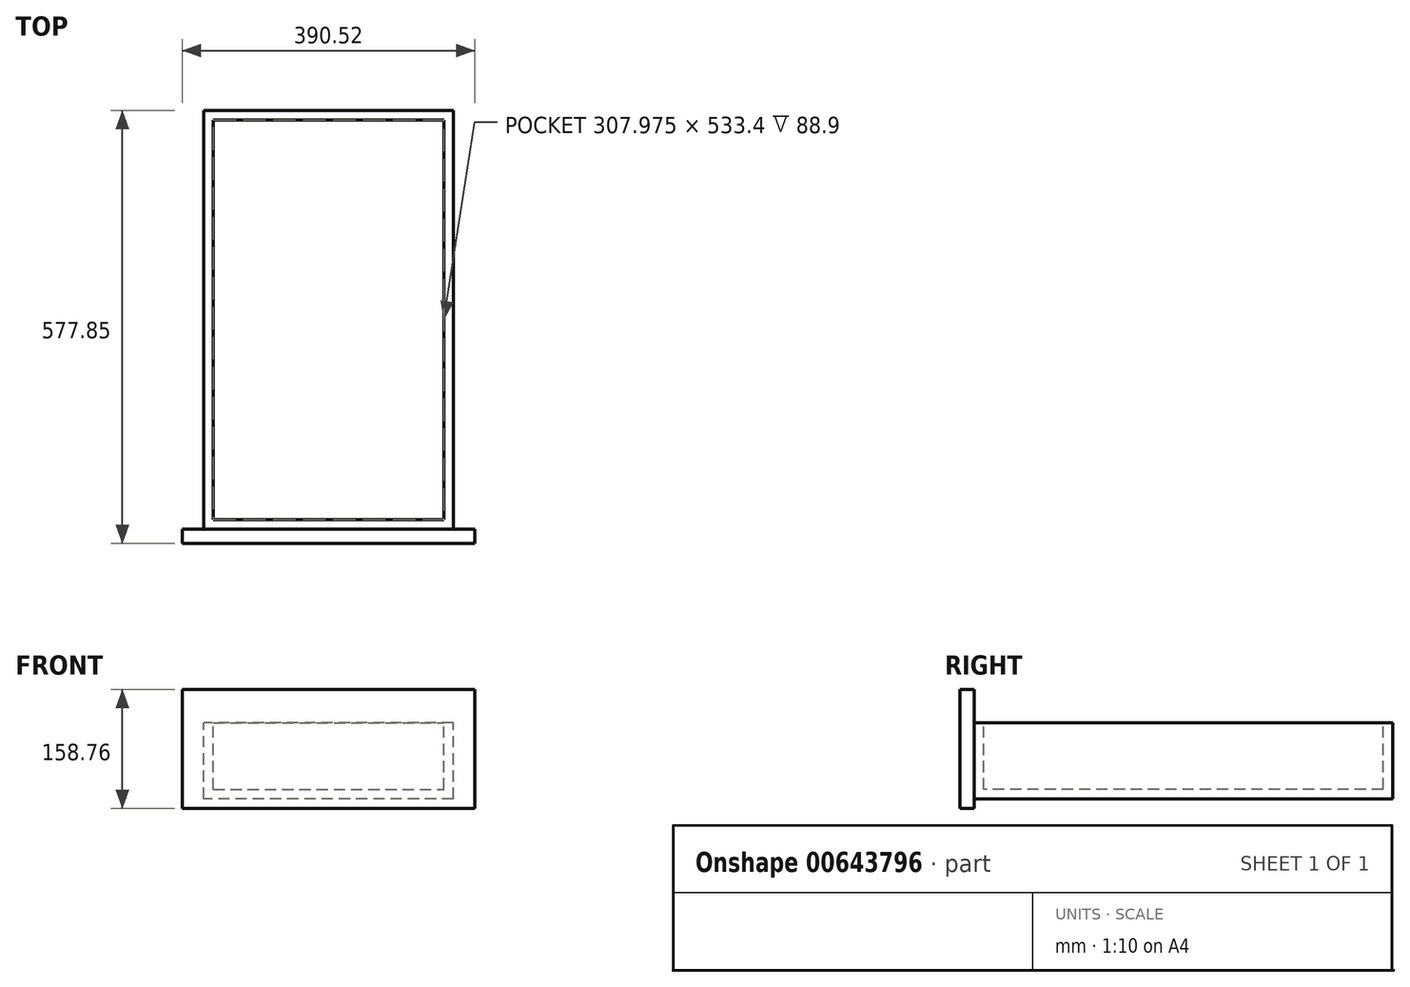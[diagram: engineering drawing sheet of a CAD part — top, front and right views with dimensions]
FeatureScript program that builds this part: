
annotation { "Feature Type Name" : "Feature", "Feature Type Description" : "" }
export const myFeature = defineFeature(function(context is Context, id is Id, definition is map)
    precondition{}
    {
        {
            var Q0;
            Q0=qCreatedBy(makeId("Front.planeOp"),FACE);
            var sketch = newSketch(context, id + "F0", { "sketchPlane" : qUnion([Q0])});
            skLineSegment(sketch, "E0.bottom", {"start": v(-195.26, 79.38) * mm, "end": v(195.26, 79.38) * mm});
            skLineSegment(sketch, "E0.top", {"start": v(-195.26, -79.38) * mm, "end": v(195.26, -79.38) * mm});
            skLineSegment(sketch, "E0.left", {"start": v(-195.26, 79.38) * mm, "end": v(-195.26, -79.38) * mm});
            skLineSegment(sketch, "E0.right", {"start": v(195.26, 79.37) * mm, "end": v(195.26, -79.38) * mm});
            skPoint(sketch, "E0.middle", {"position": v(0, 0) * mm});
            skSolve(sketch);
        }
        {
            var Q0;
            Q0=makeQuery(id+"F0.imprint","IMPRINT",FACE,{"disambiguationData":[TD([[makeQuery(id+"F0.imprint","IMPRINT",EDGE,{"derivedFrom":sQuery(id+"F0.wireOp",EDGE,"E0.bottom")}),-1.0]])]});
            extrude(context, id + "F1", {"entities" : qUnion([Q0]), "depth" : 19.05 * mm, "offsetDistance" : 25.4 * mm});
        }
        {
            var Q0;
            Q0=makeQuery(id+"F1.opExtrude","CAP_FACE",FACE,{"disambiguationData":[OSD([sQuery(id+"F0.wireOp",EDGE,"E0.bottom"),sQuery(id+"F0.wireOp",EDGE,"E0.top"),sQuery(id+"F0.wireOp",EDGE,"E0.left"),sQuery(id+"F0.wireOp",EDGE,"E0.right")])],"isStart":true});
            var sketch = newSketch(context, id + "F2", { "sketchPlane" : qUnion([Q0])});
            skLineSegment(sketch, "E1", {"start": v(0, -79.38) * mm, "end": v(0, -66.67) * mm});
            skPoint(sketch, "E1.endSnap0", {"position": v(0, -79.38) * mm});
            skLineSegment(sketch, "E2", {"start": v(0, -66.67) * mm, "end": v(0, -15.87) * mm});
            skLineSegment(sketch, "E3.bottom", {"start": v(-166.69, -66.67) * mm, "end": v(166.69, -66.67) * mm});
            skLineSegment(sketch, "E3.top", {"start": v(-166.69, 34.93) * mm, "end": v(166.69, 34.93) * mm});
            skLineSegment(sketch, "E3.left", {"start": v(-166.69, -66.67) * mm, "end": v(-166.69, 34.93) * mm});
            skLineSegment(sketch, "E3.right", {"start": v(166.69, -66.67) * mm, "end": v(166.69, 34.93) * mm});
            skPoint(sketch, "E3.middle", {"position": v(0, -15.87) * mm});
            skSolve(sketch);
        }
        {
            var Q0;
            Q0=makeQuery(id+"F2.imprint","IMPRINT",FACE,{"disambiguationData":[TD([[makeQuery(id+"F2.imprint","IMPRINT",EDGE,{"derivedFrom":sQuery(id+"F2.wireOp",EDGE,"E3.top")}),-1.0]])]});
            extrude(context, id + "F3", {"entities" : qUnion([Q0]), "operationType" : NewBodyOperationType.ADD, "depth" : 558.8 * mm, "offsetDistance" : 25.4 * mm});
        }
        {
            var Q0;
            Q0=makeQuery(id+"F3.opExtrude","SWEPT_FACE",FACE,{"disambiguationData":[OSD([sQuery(id+"F2.wireOp",EDGE,"E3.top")])]});
            var sketch = newSketch(context, id + "F4", { "sketchPlane" : qUnion([Q0])});
            skLineSegment(sketch, "E4.bottom", {"start": v(-153.99, 546.1) * mm, "end": v(153.99, 546.1) * mm});
            skLineSegment(sketch, "E4.top", {"start": v(-153.99, 12.7) * mm, "end": v(153.99, 12.7) * mm});
            skLineSegment(sketch, "E4.left", {"start": v(-153.99, 546.1) * mm, "end": v(-153.99, 12.7) * mm});
            skLineSegment(sketch, "E4.right", {"start": v(153.99, 546.1) * mm, "end": v(153.99, 12.7) * mm});
            skPoint(sketch, "E4.middle", {"position": v(0, 279.4) * mm});
            skPoint(sketch, "E4.middle.positionSnap0", {"position": v(-166.69, 279.4) * mm});
            skPoint(sketch, "E4.centerSnap0", {"position": v(-166.69, 279.4) * mm});
            skSolve(sketch);
        }
        {
            var Q0;
            Q0=makeQuery(id+"F4.imprint","IMPRINT",FACE,{"disambiguationData":[TD([[makeQuery(id+"F4.imprint","IMPRINT",EDGE,{"derivedFrom":sQuery(id+"F4.wireOp",EDGE,"E4.bottom")}),-1.0]])]});
            extrude(context, id + "F5", {"entities" : qUnion([Q0]), "operationType" : NewBodyOperationType.REMOVE, "oppositeDirection" : true, "depth" : 88.9 * mm, "offsetDistance" : 25.4 * mm});
        }
    });
